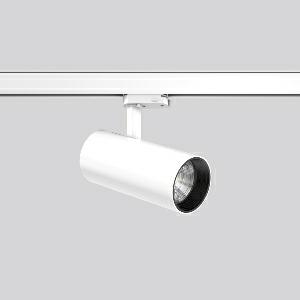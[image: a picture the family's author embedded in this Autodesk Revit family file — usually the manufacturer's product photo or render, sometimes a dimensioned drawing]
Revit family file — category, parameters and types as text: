
# Revit family: deecos_s_mini_742209_002_76_996d
name_source: partatom
category: Lighting Fixtures
units: mm (PartAtom-declared; Revit-internal decimal feet)

## family parameters
Cut with Voids When Loaded = No
Host = Face
Light Source = No
Part Type = Normal
Room Calculation Point = No
Round Connector Dimension = Use Diameter
Shared = No

## types (1)
- DEECOS S mini (1 x LED Modul 930, 3250 lm, 3000)
    Apparent Load = 29 VA
    Approval mark = CE
    CIE Flux Codes = 80 99 100 100 100
    Color Rendering = 90
    Color Temperature = 3000
    Default Elevation = 1800 mm
    Description = Series: DEECOS S mini
LED surface-mounted projector in modern design with no visible cooling ribs. Housing: die-cast aluminium, powder-coated. Rotation range: 356°. Swivel range: 90°. Black plastic ring and recessed LED to prevent glare from the side. Optical assembly with lens made of plastic (polycarbonate) for the best homogeneous light distribution - can be changed without tools. Best colour rendering index Ra>90. With adapter for RZB 3-circuit DALI tracks. Suitable for Track on ceiling, Wall track. High quality converter without flickering and stroboscopic effect. The following accessories can be mounted without use of tools: interchangeable lenses, decorative glasses, honeycomb louvre, clear and frosted diffusers, white interchangeable plastic ring. 
Colour: traffic white, matt (RAL 9016)
Diameter: 87 mm
Height: 214 mm
Lamp: LED
Socket: without socket
Colour temperature: 3000K
Colour rendering index (CRI): 92
System power: 29 W
Rated luminous flux: 3250 lm
Luminous efficiency: 112 lm/W
Control gear: Converter, dimmable, DALI
Protection class: I
Type of protection: IP 20
    Height = 214 mm
    Lamp = 1 x LED Modul 930
    Lamp Light Flux = 3250 lm
    Lamp count = 1
    Length = 87 mm
    Lifetime = 50000 h
    Luminous efficacy = 112 lm/W
    Manufacturer = RZB
    ModVariant = No
    Model = 742209.002.76
    Mounting Place = Ceiling
    Mounting Type = Rail mounted
    Number of Poles = 1
    OnlyDefault = Yes
    Power Factor = 1
    Product Name = DEECOS S mini
    Product group = Track mounted projectors
    ProductGroupID = 301
    Protection Class = Protection class I
    Protection Degree = IP 20
    RLX_Detail_Level = 1
    RLX_Emergency_Light_Flux = 0 lm
    RLX_Emergency_Type = 0
    RLX_Emergency_Type_DB = No
    RlxData = <blob elided: 35113 chars, md5=f149b7e3>
    Socket = socket
    Standby Power = 0 W
    System Light Flux = 3250 lm
    System Power = 29 W
    Type Comments = Product without accessories
    Type Image = 741930.002.jpg
    URL = http://relux.com
    VarID = ---
    Voltage = 230 V
    Voltage Range = 220-240 V
    Weight = 0.00 kg
    Width = 0 mm  [stored 0 ft]

note: [stored X ft] marks values corroborated as IEEE doubles in the binary element streams (Revit-internal decimal feet)

## geometry (parser evidence)
native form markers: Blend x4, Sweep x11
no freeform markers — native parametric forms only
